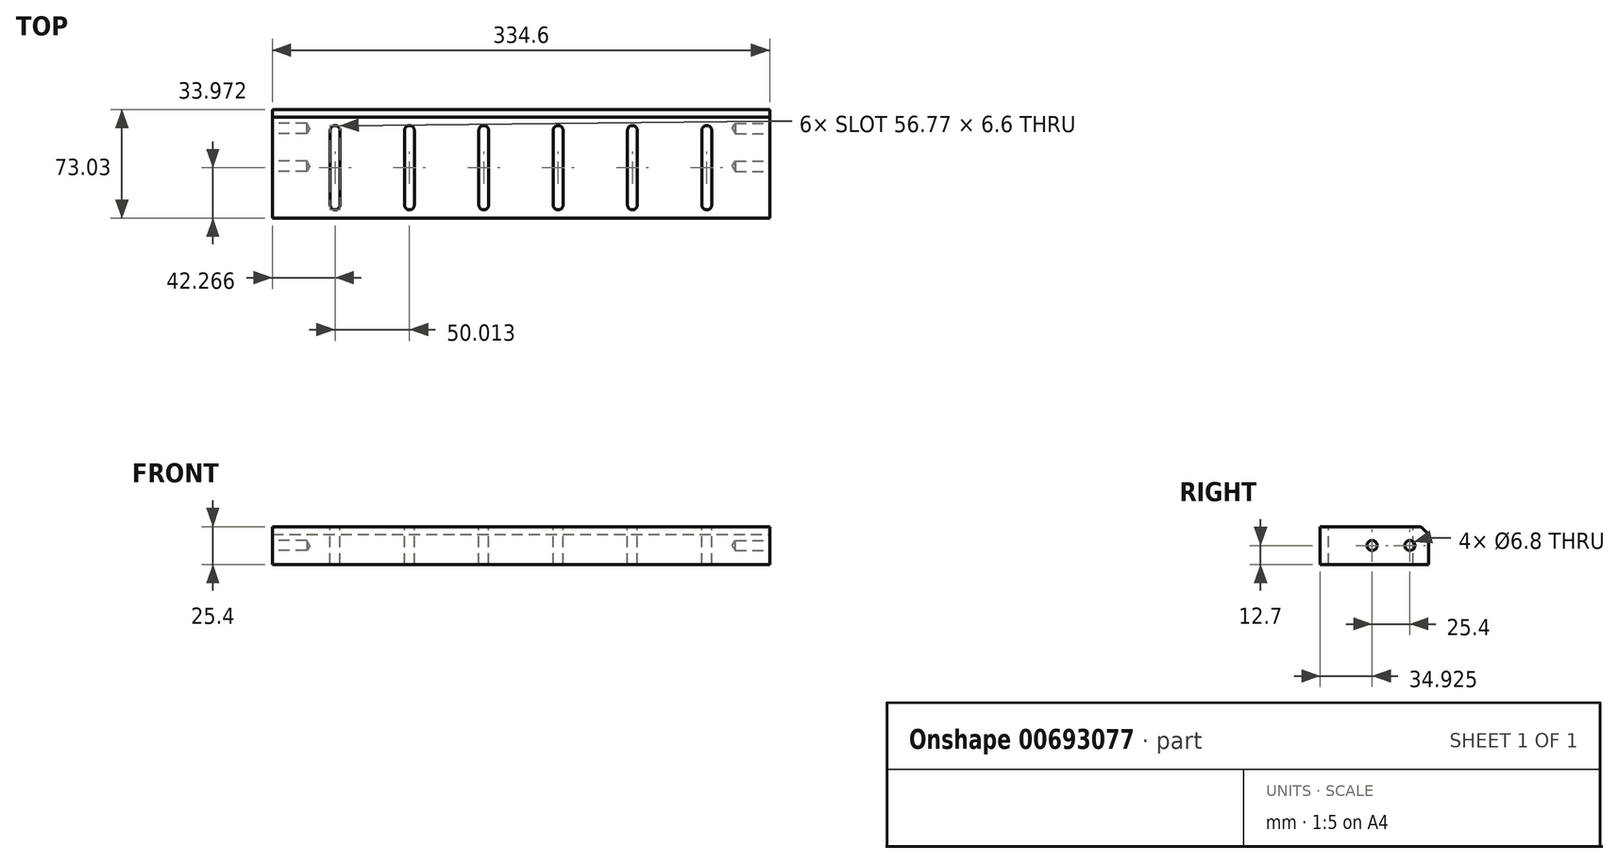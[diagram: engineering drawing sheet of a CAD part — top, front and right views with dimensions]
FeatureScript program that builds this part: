
annotation { "Feature Type Name" : "Feature", "Feature Type Description" : "" }
export const myFeature = defineFeature(function(context is Context, id is Id, definition is map)
    precondition{}
    {
        {
            var Q0;
            Q0=qCreatedBy(makeId("Top.planeOp"),FACE);
            var sketch = newSketch(context, id + "F0", { "sketchPlane" : qUnion([Q0])});
            skLineSegment(sketch, "E0.bottom", {"start": v(-2.71, 0) * mm, "end": v(331.89, 0) * mm});
            skLineSegment(sketch, "E0.top", {"start": v(-2.71, 73.03) * mm, "end": v(331.89, 73.03) * mm});
            skLineSegment(sketch, "E0.left", {"start": v(-2.71, 0) * mm, "end": v(-2.71, 73.03) * mm});
            skLineSegment(sketch, "E0.right", {"start": v(331.89, 0) * mm, "end": v(331.89, 73.03) * mm});
            skSolve(sketch);
        }
        {
            var Q0;
            Q0=makeQuery(id+"F0.imprint","IMPRINT",FACE,{"disambiguationData":[TD([[makeQuery(id+"F0.imprint","IMPRINT",EDGE,{"derivedFrom":sQuery(id+"F0.wireOp",EDGE,"E0.bottom")}),1.0]])]});
            extrude(context, id + "F1", {"entities" : qUnion([Q0]), "depth" : 25.4 * mm, "offsetDistance" : 25.4 * mm});
        }
        {
            var Q0;
            Q0=makeQuery(id+"F1.opExtrude","CAP_EDGE",EDGE,{"disambiguationData":[OSD([sQuery(id+"F0.wireOp",EDGE,"E0.top")])],"isStart":false});
            chamfer(context, id + "F2", {"entities" : qUnion([Q0]), "width" : 5.08 * mm, "tangentPropagation" : true});
        }
        {
            var Q0;
            Q0=makeQuery(id+"F1.opExtrude","SWEPT_FACE",FACE,{"disambiguationData":[OSD([sQuery(id+"F0.wireOp",EDGE,"E0.right")])]});
            var sketch = newSketch(context, id + "F3", { "sketchPlane" : qUnion([Q0])});
            skLineSegment(sketch, "E1", {"start": v(73.02, 12.7) * mm, "end": v(60.32, 12.7) * mm});
            skPoint(sketch, "E1.startSnap0", {"position": v(0, 12.7) * mm});
            skLineSegment(sketch, "E2", {"start": v(60.32, 12.7) * mm, "end": v(34.92, 12.7) * mm});
            skSolve(sketch);
        }
        {
            var Q0;
            Q0=sQuery(id+"F3.wireOp",VERTEX,"E2.end");
            var Q1;
            Q1=sQuery(id+"F3.wireOp",VERTEX,"E2.start");
            var Q2;
            Q2=makeQuery(id+"F1.opExtrude","SWEPT_BODY",BODY,{"disambiguationData":[OSD([sQuery(id+"F0.wireOp",EDGE,"E0.bottom"),sQuery(id+"F0.wireOp",EDGE,"E0.top"),sQuery(id+"F0.wireOp",EDGE,"E0.left"),sQuery(id+"F0.wireOp",EDGE,"E0.right")])]});
            hole(context, id + "F4", {"style" : HoleStyle.SIMPLE, "endStyle" : HoleEndStyle.BLIND, "standardTappedOrClearance" : lookupTablePath({ "standard" : "ISO", "engagement" : "75%", "pitch" : "1.25 mm", "size" : "M8", "type" : "Tapped" }), "standardBlindInLast" : lookupTablePath({ "standard" : "ISO", "engagement" : "75%", "pitch" : "1.25 mm", "size" : "M8", "type" : "Tapped" }), "holeDiameter" : 6.8 * mm, "majorDiameter" : 8 * mm, "showTappedDepth" : true, "holeDepth" : 23.15 * mm, "tappedDepth" : 19.4 * mm, "tapClearance" : 3, "locations" : qUnion([Q0, Q1]), "scope" : qUnion([Q2])});
        }
        {
            var Q0;
            Q0=makeQuery(id+"F1.opExtrude","SWEPT_FACE",FACE,{"disambiguationData":[OSD([sQuery(id+"F0.wireOp",EDGE,"E0.left")])]});
            var sketch = newSketch(context, id + "F5", { "sketchPlane" : qUnion([Q0])});
            skPoint(sketch, "E3.endSnap0", {"position": v(-73.03, 10.16) * mm});
            skLineSegment(sketch, "E4", {"start": v(-73.03, 12.7) * mm, "end": v(-60.33, 12.7) * mm});
            skLineSegment(sketch, "E5", {"start": v(-60.33, 12.7) * mm, "end": v(-34.92, 12.7) * mm});
            skSolve(sketch);
        }
        {
            var Q0;
            Q0=sQuery(id+"F5.wireOp",VERTEX,"E5.start");
            var Q1;
            Q1=sQuery(id+"F5.wireOp",VERTEX,"E5.end");
            var Q2;
            Q2=makeQuery(id+"F1.opExtrude","SWEPT_BODY",BODY,{"disambiguationData":[OSD([sQuery(id+"F0.wireOp",EDGE,"E0.bottom"),sQuery(id+"F0.wireOp",EDGE,"E0.top"),sQuery(id+"F0.wireOp",EDGE,"E0.left"),sQuery(id+"F0.wireOp",EDGE,"E0.right")])]});
            hole(context, id + "F6", {"style" : HoleStyle.SIMPLE, "endStyle" : HoleEndStyle.BLIND, "standardTappedOrClearance" : lookupTablePath({ "standard" : "ISO", "engagement" : "75%", "pitch" : "1.25 mm", "size" : "M8", "type" : "Tapped" }), "standardBlindInLast" : lookupTablePath({ "standard" : "ISO", "engagement" : "75%", "pitch" : "1.25 mm", "size" : "M8", "type" : "Tapped" }), "holeDiameter" : 6.8 * mm, "majorDiameter" : 8 * mm, "showTappedDepth" : true, "holeDepth" : 23.14 * mm, "tappedDepth" : 19.4 * mm, "tapClearance" : 3, "locations" : qUnion([Q0, Q1]), "scope" : qUnion([Q2])});
        }
        {
            var Q0;
            Q0=makeQuery(id+"F1.opExtrude","CAP_FACE",FACE,{"disambiguationData":[OSD([sQuery(id+"F0.wireOp",EDGE,"E0.bottom"),sQuery(id+"F0.wireOp",EDGE,"E0.top"),sQuery(id+"F0.wireOp",EDGE,"E0.left"),sQuery(id+"F0.wireOp",EDGE,"E0.right")])],"isStart":false});
            var sketch = newSketch(context, id + "F7", { "sketchPlane" : qUnion([Q0])});
            skLineSegment(sketch, "E6", {"start": v(164.59, 0) * mm, "end": v(164.59, 8.9) * mm});
            skLineSegment(sketch, "E7", {"start": v(164.59, 0) * mm, "end": v(164.59, 8.89) * mm});
            skLineSegment(sketch, "E8", {"start": v(164.59, 8.9) * mm, "end": v(139.58, 8.89) * mm});
            skLineSegment(sketch, "E9", {"start": v(164.59, 67.95) * mm, "end": v(164.59, 59.06) * mm});
            skLineSegment(sketch, "E10", {"start": v(164.59, 8.9) * mm, "end": v(164.59, 59.06) * mm});
            skLineSegment(sketch, "E11", {"start": v(164.59, 33.97) * mm, "end": v(145.67, 33.97) * mm});
            skLineSegment(sketch, "E12.MirrorCS", {"start": v(164.59, 59.06) * mm, "end": v(139.58, 59.06) * mm});
            skLineSegment(sketch, "E13", {"start": v(139.58, 8.89) * mm, "end": v(89.57, 8.89) * mm});
            skLineSegment(sketch, "E14", {"start": v(89.57, 8.89) * mm, "end": v(39.56, 8.89) * mm});
            skLineSegment(sketch, "E15.MirrorCS", {"start": v(139.58, 59.06) * mm, "end": v(89.57, 59.06) * mm});
            skLineSegment(sketch, "E16.MirrorCS", {"start": v(89.57, 59.06) * mm, "end": v(39.56, 59.06) * mm});
            skLineSegment(sketch, "E17.MirrorCS", {"start": v(164.59, 8.9) * mm, "end": v(189.6, 8.89) * mm});
            skLineSegment(sketch, "E18.MirrorCS", {"start": v(164.59, 59.06) * mm, "end": v(189.6, 59.06) * mm});
            skLineSegment(sketch, "E19.MirrorCS", {"start": v(189.6, 59.06) * mm, "end": v(239.6, 59.06) * mm});
            skLineSegment(sketch, "E20.MirrorCS", {"start": v(189.6, 8.89) * mm, "end": v(239.6, 8.89) * mm});
            skLineSegment(sketch, "E21.MirrorCS", {"start": v(239.6, 8.89) * mm, "end": v(289.62, 8.89) * mm});
            skLineSegment(sketch, "E22.MirrorCS", {"start": v(239.6, 59.06) * mm, "end": v(289.62, 59.06) * mm});
            skSolve(sketch);
        }
        {
            var Q0;
            Q0=sQuery(id+"F7.wireOp",VERTEX,"bd394d0c-9067-4817-904b-b2741602010b0.MirrorCS.end");
            var Q1;
            Q1=sQuery(id+"F7.wireOp",VERTEX,"be71b2b8-ef01-4875-8472-178ad34bbe620.MirrorCS.end");
            var Q2;
            Q2=sQuery(id+"F7.wireOp",VERTEX,"E21.MirrorCS.end");
            var Q3;
            Q3=sQuery(id+"F7.wireOp",VERTEX,"E22.MirrorCS.end");
            var Q4;
            Q4=makeQuery(id+"F1.opExtrude","SWEPT_BODY",BODY,{"disambiguationData":[OSD([sQuery(id+"F0.wireOp",EDGE,"E0.bottom"),sQuery(id+"F0.wireOp",EDGE,"E0.top"),sQuery(id+"F0.wireOp",EDGE,"E0.left"),sQuery(id+"F0.wireOp",EDGE,"E0.right")])]});
            hole(context, id + "F8", {"style" : HoleStyle.SIMPLE, "endStyle" : HoleEndStyle.THROUGH, "standardTappedOrClearance" : lookupTablePath({ "standard" : "ISO", "fit" : "Normal", "size" : "M6", "type" : "Clearance" }), "standardBlindInLast" : lookupTablePath({ "fit" : "Standard", "standard" : "ISO", "size" : "M6", "type" : "Clearance" }), "holeDiameter" : 6.6 * mm, "majorDiameter" : 6.35 * mm, "tappedDepth" : 19.38 * mm, "tapClearance" : 3, "locations" : qUnion([Q0, Q1, Q2, Q3]), "scope" : qUnion([Q4])});
        }
        {
            var Q0;
            Q0=makeQuery(id+"F1.opExtrude","CAP_FACE",FACE,{"disambiguationData":[OSD([sQuery(id+"F0.wireOp",EDGE,"E0.bottom"),sQuery(id+"F0.wireOp",EDGE,"E0.top"),sQuery(id+"F0.wireOp",EDGE,"E0.left"),sQuery(id+"F0.wireOp",EDGE,"E0.right")])],"isStart":false});
            var sketch = newSketch(context, id + "F9", { "sketchPlane" : qUnion([Q0])});
            skLineSegment(sketch, "E23", {"start": v(289.62, 8.89) * mm, "end": v(292.92, 8.89) * mm});
            skLineSegment(sketch, "E24", {"start": v(292.92, 8.89) * mm, "end": v(292.92, 59.06) * mm});
            skLineSegment(sketch, "E25", {"start": v(292.92, 59.06) * mm, "end": v(286.32, 59.06) * mm});
            skLineSegment(sketch, "E26", {"start": v(286.32, 59.06) * mm, "end": v(286.32, 8.89) * mm});
            skLineSegment(sketch, "E27", {"start": v(286.32, 8.89) * mm, "end": v(289.62, 8.89) * mm});
            skSolve(sketch);
        }
        {
            var Q0;
            {var subQ0=sQuery(id+"F9.wireOp",EDGE,"E24");Q0=makeQuery(id+"F9.imprint","IMPRINT",FACE,{"disambiguationData":[TD([[makeQuery(id+"F9.imprint","IMPRINT",EDGE,{"derivedFrom":subQ0}),1.0]])]});}
            extrude(context, id + "F10", {"entities" : qUnion([Q0]), "operationType" : NewBodyOperationType.REMOVE, "oppositeDirection" : true, "depth" : 25.4 * mm, "offsetDistance" : 25.4 * mm});
        }
        {
            var Q0;
            Q0=makeQuery(id+"F1.opExtrude","CAP_FACE",FACE,{"disambiguationData":[OSD([sQuery(id+"F0.wireOp",EDGE,"E0.bottom"),sQuery(id+"F0.wireOp",EDGE,"E0.top"),sQuery(id+"F0.wireOp",EDGE,"E0.left"),sQuery(id+"F0.wireOp",EDGE,"E0.right")])],"isStart":false});
            var sketch = newSketch(context, id + "F11", { "sketchPlane" : qUnion([Q0])});
            skArc(sketch, "E28.0", {"start": v(286.32, 8.89) * mm, "mid": v(289.62, 5.59) * mm, "end": v(292.92, 8.89) * mm});
            skLineSegment(sketch, "E29.0", {"start": v(286.32, 59.06) * mm, "end": v(286.32, 8.89) * mm});
            skLineSegment(sketch, "E30.0", {"start": v(292.92, 8.89) * mm, "end": v(292.92, 59.06) * mm});
            skArc(sketch, "E31.0", {"start": v(292.92, 59.06) * mm, "mid": v(289.62, 62.36) * mm, "end": v(286.32, 59.06) * mm});
            skLineSegment(sketch, "E32.1.0.0", {"start": v(242.9, 8.89) * mm, "end": v(242.9, 59.06) * mm});
            skArc(sketch, "E32.1.0.1", {"start": v(236.3, 8.89) * mm, "mid": v(239.6, 5.59) * mm, "end": v(242.9, 8.89) * mm});
            skLineSegment(sketch, "E32.1.0.2", {"start": v(236.3, 59.06) * mm, "end": v(236.3, 8.89) * mm});
            skArc(sketch, "E32.1.0.3", {"start": v(242.9, 59.06) * mm, "mid": v(239.6, 62.36) * mm, "end": v(236.3, 59.06) * mm});
            skLineSegment(sketch, "E32.2.0.0", {"start": v(192.9, 8.89) * mm, "end": v(192.9, 59.06) * mm});
            skArc(sketch, "E32.2.0.1", {"start": v(186.3, 8.89) * mm, "mid": v(189.6, 5.59) * mm, "end": v(192.9, 8.89) * mm});
            skLineSegment(sketch, "E32.2.0.2", {"start": v(186.3, 59.06) * mm, "end": v(186.3, 8.89) * mm});
            skArc(sketch, "E32.2.0.3", {"start": v(192.9, 59.06) * mm, "mid": v(189.6, 62.36) * mm, "end": v(186.3, 59.06) * mm});
            skLineSegment(sketch, "E32.3.0.0", {"start": v(142.88, 8.89) * mm, "end": v(142.88, 59.06) * mm});
            skArc(sketch, "E32.3.0.1", {"start": v(136.28, 8.89) * mm, "mid": v(139.58, 5.59) * mm, "end": v(142.88, 8.89) * mm});
            skLineSegment(sketch, "E32.3.0.2", {"start": v(136.28, 59.06) * mm, "end": v(136.28, 8.89) * mm});
            skArc(sketch, "E32.3.0.3", {"start": v(142.88, 59.06) * mm, "mid": v(139.58, 62.36) * mm, "end": v(136.28, 59.06) * mm});
            skLineSegment(sketch, "E32.4.0.0", {"start": v(92.87, 8.89) * mm, "end": v(92.87, 59.06) * mm});
            skArc(sketch, "E32.4.0.1", {"start": v(86.27, 8.89) * mm, "mid": v(89.57, 5.59) * mm, "end": v(92.87, 8.89) * mm});
            skLineSegment(sketch, "E32.4.0.2", {"start": v(86.27, 59.06) * mm, "end": v(86.27, 8.89) * mm});
            skArc(sketch, "E32.4.0.3", {"start": v(92.87, 59.06) * mm, "mid": v(89.57, 62.36) * mm, "end": v(86.27, 59.06) * mm});
            skLineSegment(sketch, "E32.5.0.0", {"start": v(42.86, 8.89) * mm, "end": v(42.86, 59.06) * mm});
            skArc(sketch, "E32.5.0.1", {"start": v(36.26, 8.89) * mm, "mid": v(39.56, 5.59) * mm, "end": v(42.86, 8.89) * mm});
            skLineSegment(sketch, "E32.5.0.2", {"start": v(36.26, 59.06) * mm, "end": v(36.26, 8.89) * mm});
            skArc(sketch, "E32.5.0.3", {"start": v(42.86, 59.06) * mm, "mid": v(39.56, 62.36) * mm, "end": v(36.26, 59.06) * mm});
            skLineSegment(sketch, "E32.direction1", {"start": v(292.92, 8.89) * mm, "end": v(242.9, 8.89) * mm, "construction": true});
            skSolve(sketch);
        }
        {
            var Q0;
            Q0=makeQuery(id+"F11.imprint","IMPRINT",FACE,{"disambiguationData":[TD([[makeQuery(id+"F11.imprint","IMPRINT",EDGE,{"derivedFrom":sQuery(id+"F11.wireOp",EDGE,"E32.1.0.0")}),1.0]])]});
            var Q1;
            Q1=makeQuery(id+"F11.imprint","IMPRINT",FACE,{"disambiguationData":[TD([[makeQuery(id+"F11.imprint","IMPRINT",EDGE,{"derivedFrom":sQuery(id+"F11.wireOp",EDGE,"E32.2.0.0")}),1.0]])]});
            var Q2;
            Q2=makeQuery(id+"F11.imprint","IMPRINT",FACE,{"disambiguationData":[TD([[makeQuery(id+"F11.imprint","IMPRINT",EDGE,{"derivedFrom":sQuery(id+"F11.wireOp",EDGE,"E32.3.0.0")}),1.0]])]});
            var Q3;
            Q3=makeQuery(id+"F11.imprint","IMPRINT",FACE,{"disambiguationData":[TD([[makeQuery(id+"F11.imprint","IMPRINT",EDGE,{"derivedFrom":sQuery(id+"F11.wireOp",EDGE,"E32.4.0.0")}),1.0]])]});
            var Q4;
            Q4=makeQuery(id+"F11.imprint","IMPRINT",FACE,{"disambiguationData":[TD([[makeQuery(id+"F11.imprint","IMPRINT",EDGE,{"derivedFrom":sQuery(id+"F11.wireOp",EDGE,"E32.5.0.0")}),1.0]])]});
            var Q5;
            Q5=makeQuery(id+"F11.imprint","IMPRINT",FACE,{"disambiguationData":[TD([[makeQuery(id+"F11.imprint","IMPRINT",EDGE,{"derivedFrom":sQuery(id+"F11.wireOp",EDGE,"E32.6.0.0")}),1.0]])]});
            var Q6;
            Q6=makeQuery(id+"F11.imprint","IMPRINT",FACE,{"disambiguationData":[TD([[makeQuery(id+"F11.imprint","IMPRINT",EDGE,{"derivedFrom":sQuery(id+"F11.wireOp",EDGE,"E32.7.0.0")}),1.0]])]});
            extrude(context, id + "F12", {"entities" : qUnion([Q0, Q1, Q2, Q3, Q4, Q5, Q6]), "operationType" : NewBodyOperationType.REMOVE, "oppositeDirection" : true, "depth" : 25.4 * mm, "offsetDistance" : 25.4 * mm});
        }
    });
